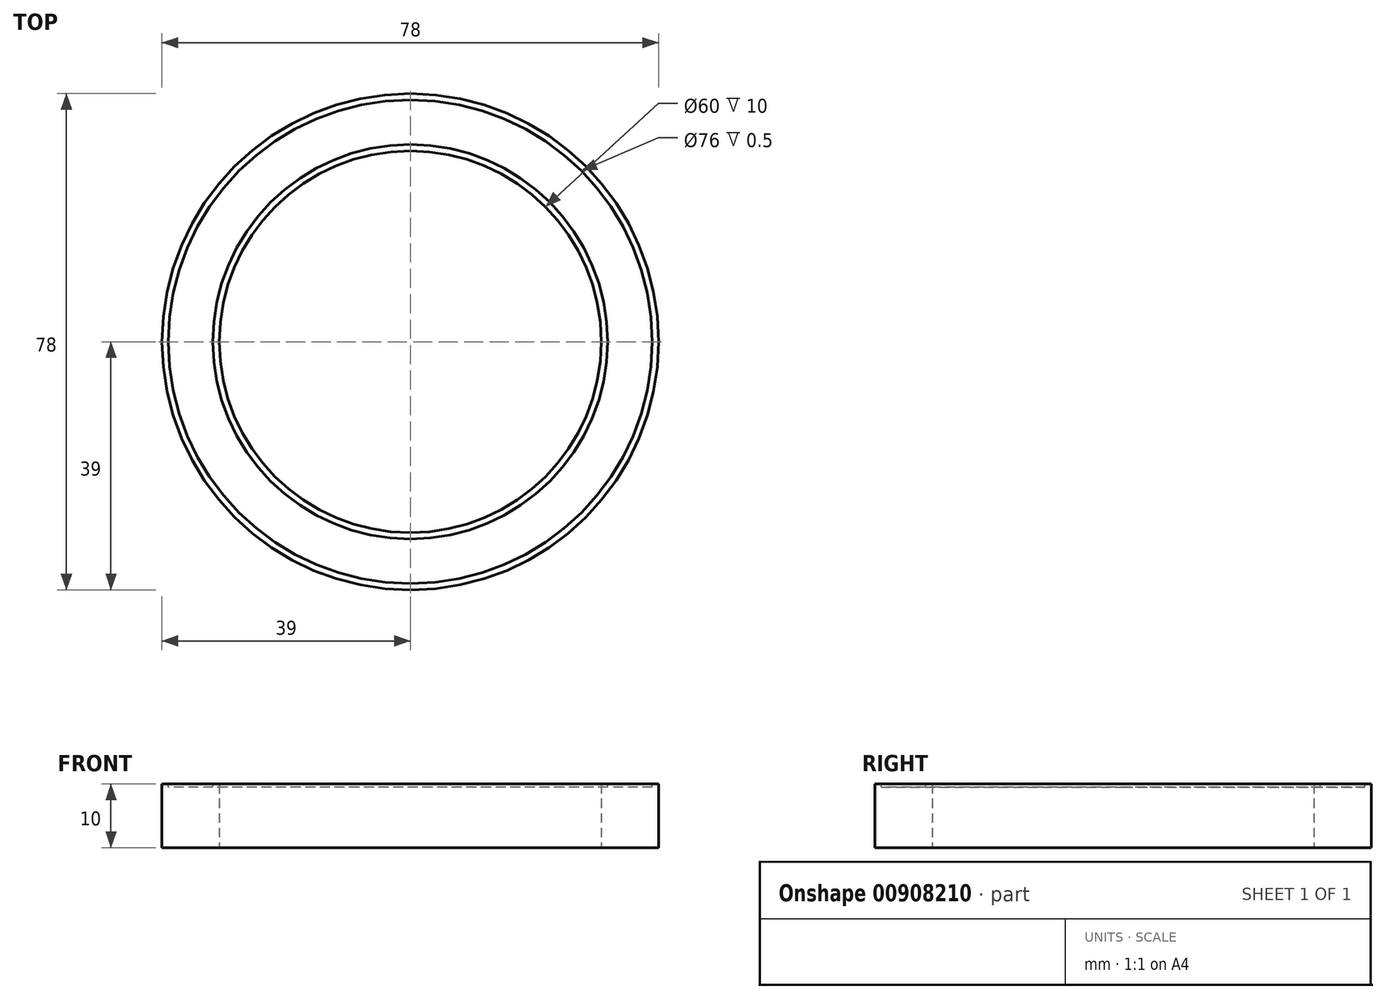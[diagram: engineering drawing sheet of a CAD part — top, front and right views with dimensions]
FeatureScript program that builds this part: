
annotation { "Feature Type Name" : "Feature", "Feature Type Description" : "" }
export const myFeature = defineFeature(function(context is Context, id is Id, definition is map)
    precondition{}
    {
        {
            var Q0;
            Q0=qCreatedBy(makeId("Top.planeOp"),FACE);
            var sketch = newSketch(context, id + "F0", { "sketchPlane" : qUnion([Q0])});
            skCircle(sketch, "E0", {"center": v(0, 0) * mm, "radius": 30 * mm});
            skCircle(sketch, "E1", {"center": v(0, 0) * mm, "radius": 39 * mm});
            skSolve(sketch);
        }
        {
            var Q0;
            Q0 = qSketchRegion(id + "F0", true);
            extrude(context, id + "F1", {"entities" : qUnion([Q0]), "depth" : 10 * mm, "offsetDistance" : 25 * mm, "symmetric" : true});
        }
        {
            var Q0;
            Q0=makeQuery(id+"F1.opExtrude","CAP_FACE",FACE,{"disambiguationData":[OSD([sQuery(id+"F0.wireOp",EDGE,"E0"),sQuery(id+"F0.wireOp",EDGE,"E1")])],"isStart":false});
            var sketch = newSketch(context, id + "F2", { "sketchPlane" : qUnion([Q0])});
            skCircle(sketch, "E2.0", {"center": v(0, 0) * mm, "radius": 38 * mm});
            skCircle(sketch, "E3.0", {"center": v(0, 0) * mm, "radius": 31 * mm});
            skSolve(sketch);
        }
        {
            var Q0;
            Q0 = qSketchRegion(id + "F2", true);
            extrude(context, id + "F3", {"entities" : qUnion([Q0]), "operationType" : NewBodyOperationType.REMOVE, "oppositeDirection" : true, "depth" : 0.5 * mm, "offsetDistance" : 25 * mm});
        }
    });
